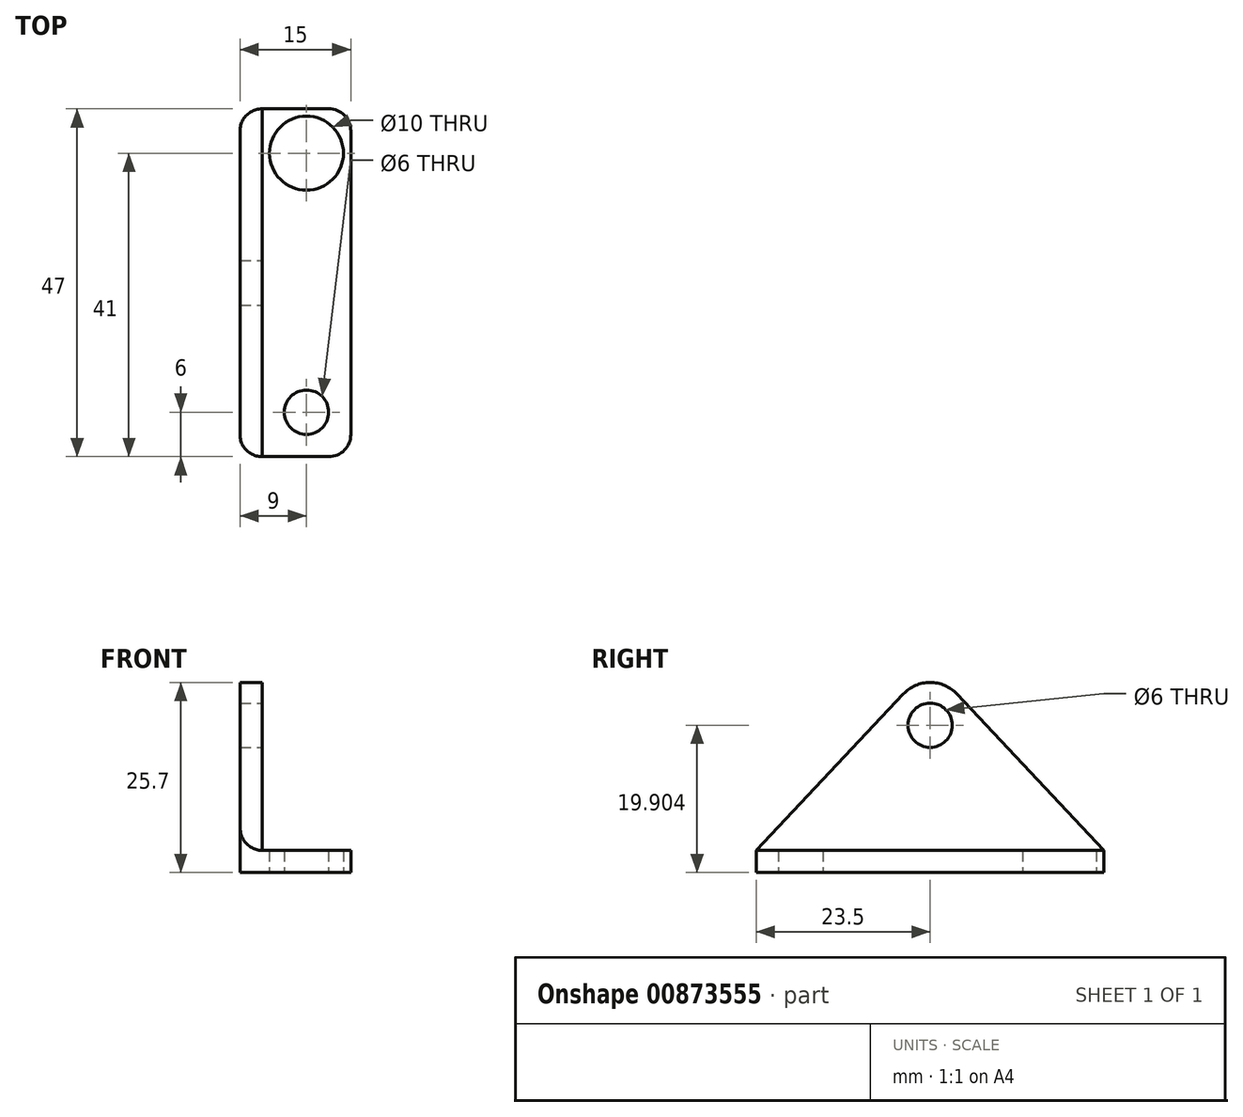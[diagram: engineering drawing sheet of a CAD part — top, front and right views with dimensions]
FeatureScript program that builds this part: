
annotation { "Feature Type Name" : "Feature", "Feature Type Description" : "" }
export const myFeature = defineFeature(function(context is Context, id is Id, definition is map)
    precondition{}
    {
        {
            var Q0;
            Q0=qCreatedBy(makeId("Top.planeOp"),FACE);
            var sketch = newSketch(context, id + "F0", { "sketchPlane" : qUnion([Q0])});
            skCircle(sketch, "E0", {"center": v(0, 0) * mm, "radius": 5 * mm});
            skCircle(sketch, "E1", {"center": v(0, -35) * mm, "radius": 3 * mm});
            skLineSegment(sketch, "E2", {"start": v(0, 6) * mm, "end": v(6, 6) * mm});
            skLineSegment(sketch, "E3", {"start": v(6, 6) * mm, "end": v(6, -41) * mm});
            skLineSegment(sketch, "E4", {"start": v(6, -41) * mm, "end": v(0, -41) * mm});
            skLineSegment(sketch, "E5.MirrorCS", {"start": v(0, 6) * mm, "end": v(-6, 6) * mm});
            skLineSegment(sketch, "E6.MirrorCS", {"start": v(-6, 6) * mm, "end": v(-6, -41) * mm});
            skLineSegment(sketch, "E7.MirrorCS", {"start": v(-6, -41) * mm, "end": v(0, -41) * mm});
            skSolve(sketch);
        }
        {
            var Q0;
            Q0 = qSketchRegion(id + "F0", true);
            extrude(context, id + "F1", {"entities" : qUnion([Q0]), "depth" : 3 * mm, "offsetDistance" : 25 * mm});
        }
        {
            var Q0;
            Q0=makeQuery(id+"F1.opExtrude","SWEPT_FACE",FACE,{"disambiguationData":[OSD([sQuery(id+"F0.wireOp",EDGE,"E6.MirrorCS")])]});
            var sketch = newSketch(context, id + "F2", { "sketchPlane" : qUnion([Q0])});
            skLineSegment(sketch, "E8.0", {"start": v(-6, 3) * mm, "end": v(-6, 0) * mm});
            skLineSegment(sketch, "E9.0", {"start": v(-6, 0) * mm, "end": v(41, 0) * mm});
            skLineSegment(sketch, "E10.0", {"start": v(41, 3) * mm, "end": v(41, 0) * mm});
            skLineSegment(sketch, "E11", {"start": v(-6, 3) * mm, "end": v(17.5, 28) * mm});
            skPoint(sketch, "E11.endSnap0", {"position": v(17.5, 3) * mm});
            skLineSegment(sketch, "E12", {"start": v(17.5, 28) * mm, "end": v(41, 3) * mm});
            skCircle(sketch, "E13", {"center": v(17.5, 19.9) * mm, "radius": 3 * mm});
            skSolve(sketch);
        }
        {
            var Q0;
            Q0 = qSketchRegion(id + "F2", true);
            extrude(context, id + "F3", {"entities" : qUnion([Q0]), "operationType" : NewBodyOperationType.ADD, "depth" : 3 * mm, "offsetDistance" : 25 * mm});
        }
        {
            var Q0;
            Q0=makeQuery(id+"F3.opExtrude","SWEPT_EDGE",EDGE,{"disambiguationData":[OSD([sQuery(id+"F2.wireOp",EDGE,"E11"),sQuery(id+"F2.wireOp",EDGE,"E12")])]});
            fillet(context, id + "F4", {"entities" : qUnion([Q0]), "radius" : 5 * mm, "tangentPropagation" : true, "allowEdgeOverflow" : false});
        }
        {
            var Q0;
            Q0=makeQuery(id+"F1.opExtrude","SWEPT_EDGE",EDGE,{"disambiguationData":[OSD([sQuery(id+"F0.wireOp",EDGE,"E3"),sQuery(id+"F0.wireOp",EDGE,"E4")])]});
            var Q1;
            Q1=makeQuery(id+"F3.opExtrude","CAP_EDGE",EDGE,{"disambiguationData":[OSD([sQuery(id+"F2.wireOp",EDGE,"E10.0")])],"isStart":false});
            var Q2;
            Q2=makeQuery(id+"F1.opExtrude","SWEPT_EDGE",EDGE,{"disambiguationData":[OSD([sQuery(id+"F0.wireOp",EDGE,"E2"),sQuery(id+"F0.wireOp",EDGE,"E3")])]});
            var Q3;
            Q3=makeQuery(id+"F3.opExtrude","CAP_EDGE",EDGE,{"disambiguationData":[OSD([sQuery(id+"F2.wireOp",EDGE,"E8.0")])],"isStart":false});
            fillet(context, id + "F5", {"entities" : qUnion([Q0, Q1, Q2, Q3]), "radius" : 3 * mm, "tangentPropagation" : true, "allowEdgeOverflow" : false});
        }
    });
